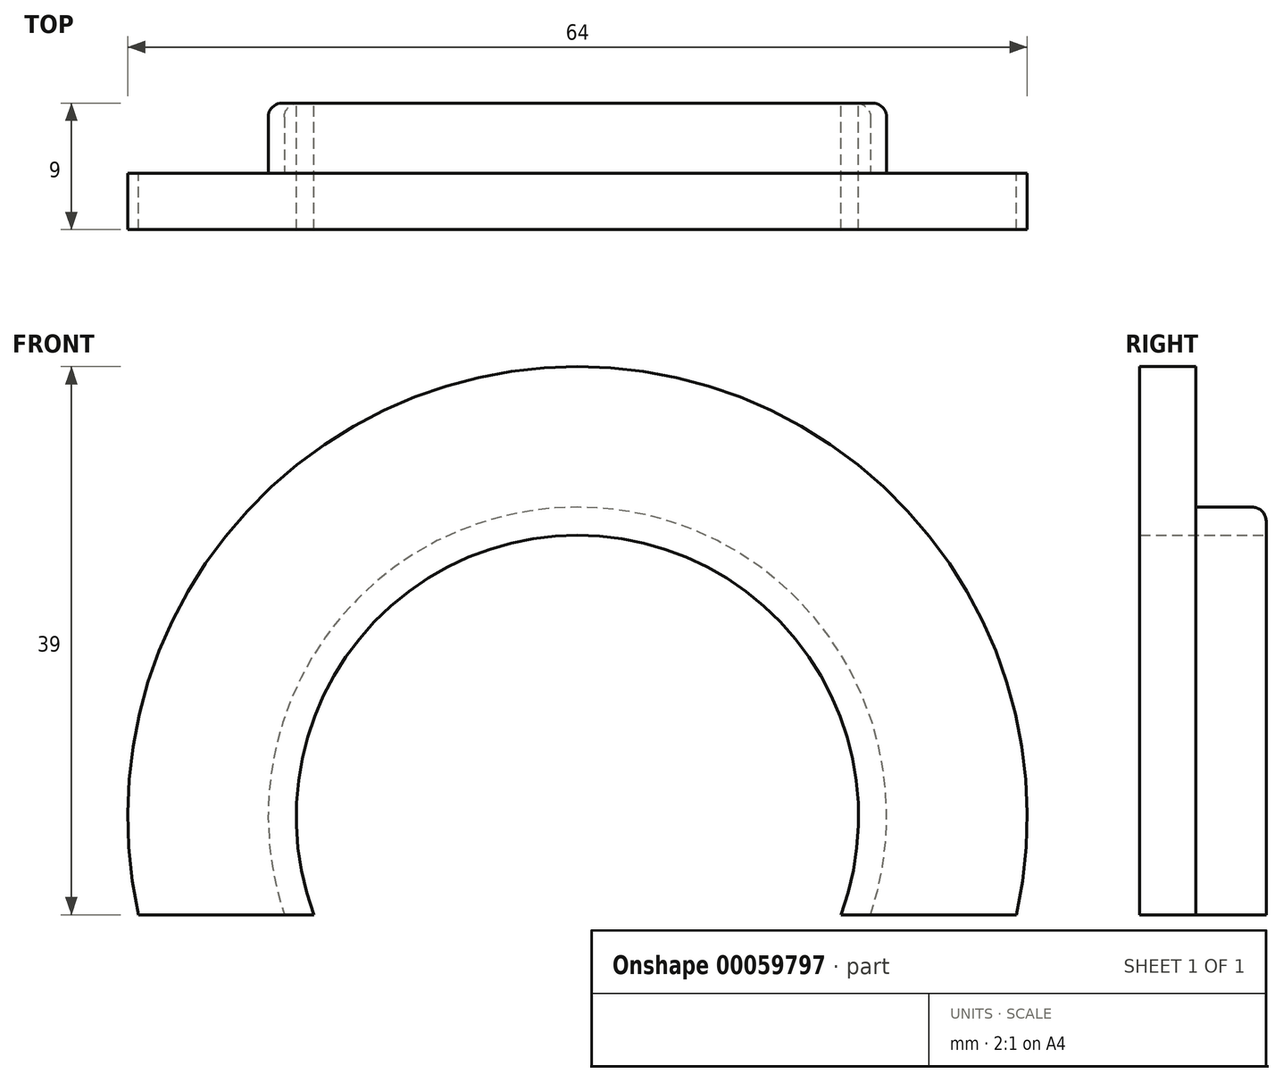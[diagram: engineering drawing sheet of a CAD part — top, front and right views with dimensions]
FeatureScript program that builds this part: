
annotation { "Feature Type Name" : "Feature", "Feature Type Description" : "" }
export const myFeature = defineFeature(function(context is Context, id is Id, definition is map)
    precondition{}
    {
        {
            var Q0;
            Q0=qCreatedBy(makeId("Front.planeOp"),FACE);
            var sketch = newSketch(context, id + "F0", { "sketchPlane" : qUnion([Q0])});
            skLineSegment(sketch, "E0", {"start": v(0, 0) * mm, "end": v(0, 7) * mm, "construction": true});
            skLineSegment(sketch, "E1", {"start": v(-100.93, 0) * mm, "end": v(99.07, 0) * mm, "construction": true});
            skCircle(sketch, "E2", {"center": v(0, 7) * mm, "radius": 22 * mm, "construction": true});
            skCircle(sketch, "E3", {"center": v(0, 7) * mm, "radius": 32 * mm, "construction": true});
            skLineSegment(sketch, "E4", {"start": v(0, 7) * mm, "end": v(0, 29) * mm, "construction": true});
            skArc(sketch, "E5", {"start": v(31.22, 0) * mm, "mid": v(0, 39) * mm, "end": v(-31.22, 0) * mm});
            skCircle(sketch, "E6", {"center": v(0, 7) * mm, "radius": 20 * mm, "construction": true});
            skArc(sketch, "E7", {"start": v(-18.73, 0) * mm, "mid": v(0, 27) * mm, "end": v(18.73, 0) * mm});
            skLineSegment(sketch, "E8", {"start": v(-18.73, 0) * mm, "end": v(-31.22, 0) * mm});
            skLineSegment(sketch, "E9", {"start": v(18.73, 0) * mm, "end": v(31.22, 0) * mm});
            skSolve(sketch);
        }
        {
            var Q0;
            Q0 = qSketchRegion(id + "F0", true);
            extrude(context, id + "F1", {"entities" : qUnion([Q0]), "depth" : 4 * mm});
        }
        {
            var Q0;
            Q0=makeQuery(id+"F1.opExtrude","CAP_FACE",FACE,{"disambiguationData":[OSD([sQuery(id+"F0.wireOp",EDGE,"E5"),sQuery(id+"F0.wireOp",EDGE,"E7"),sQuery(id+"F0.wireOp",EDGE,"E8"),sQuery(id+"F0.wireOp",EDGE,"E9")])],"isStart":true});
            var sketch = newSketch(context, id + "F2", { "sketchPlane" : qUnion([Q0])});
            skCircle(sketch, "E10", {"center": v(0, 7) * mm, "radius": 20 * mm, "construction": true});
            skCircle(sketch, "E11", {"center": v(0, 7) * mm, "radius": 22 * mm, "construction": true});
            skLineSegment(sketch, "E12", {"start": v(-18.73, 0) * mm, "end": v(-20.86, 0) * mm});
            skLineSegment(sketch, "E13", {"start": v(18.73, 0) * mm, "end": v(20.86, 0) * mm});
            skArc(sketch, "E14", {"start": v(-20.86, 0) * mm, "mid": v(0, 29) * mm, "end": v(20.86, 0) * mm});
            skArc(sketch, "E15", {"start": v(-18.73, 0) * mm, "mid": v(0, 27) * mm, "end": v(18.73, 0) * mm});
            skSolve(sketch);
        }
        {
            var Q0;
            Q0 = qSketchRegion(id + "F2", true);
            extrude(context, id + "F3", {"entities" : qUnion([Q0]), "operationType" : NewBodyOperationType.ADD, "depth" : 5 * mm});
        }
        {
            var Q0;
            Q0=makeQuery(id+"F3.opExtrude","CAP_EDGE",EDGE,{"disambiguationData":[OSD([sQuery(id+"F2.wireOp",EDGE,"E14")])],"isStart":false});
            fillet(context, id + "F4", {"entities" : qUnion([Q0]), "radius" : 1 * mm, "tangentPropagation" : true, "allowEdgeOverflow" : false});
        }
    });
